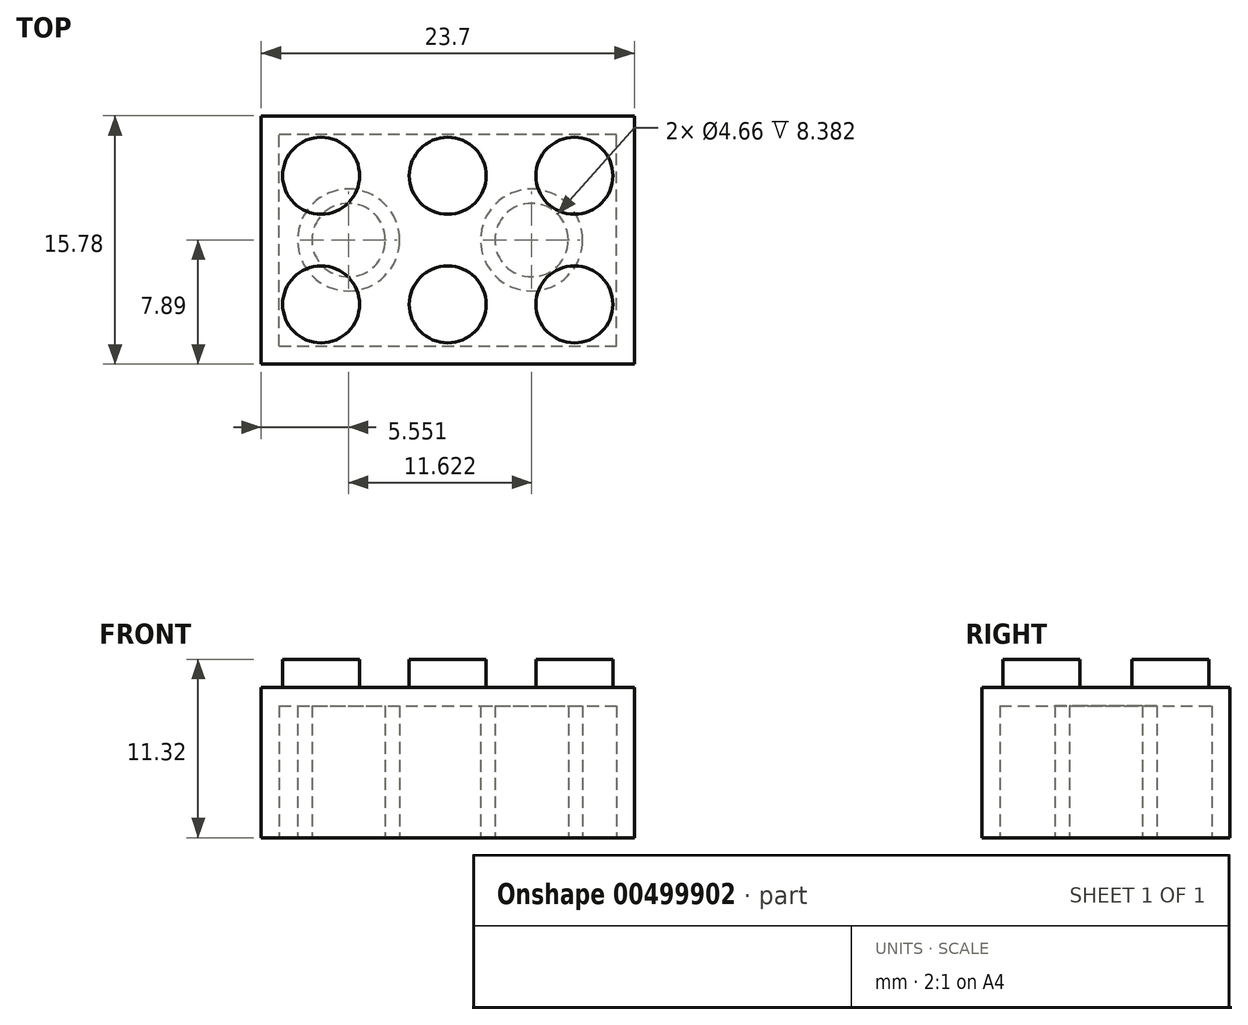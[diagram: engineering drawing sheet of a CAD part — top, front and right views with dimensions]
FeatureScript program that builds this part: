
annotation { "Feature Type Name" : "Feature", "Feature Type Description" : "" }
export const myFeature = defineFeature(function(context is Context, id is Id, definition is map)
    precondition{}
    {
        {
            var Q0;
            Q0=qCreatedBy(makeId("Top.planeOp"),FACE);
            var sketch = newSketch(context, id + "F0", { "sketchPlane" : qUnion([Q0])});
            skLineSegment(sketch, "E0.bottom", {"start": v(-11.85, 7.89) * mm, "end": v(11.85, 7.89) * mm});
            skLineSegment(sketch, "E0.top", {"start": v(-11.85, -7.89) * mm, "end": v(11.85, -7.89) * mm});
            skLineSegment(sketch, "E0.left", {"start": v(-11.85, 7.89) * mm, "end": v(-11.85, -7.89) * mm});
            skLineSegment(sketch, "E0.right", {"start": v(11.85, 7.89) * mm, "end": v(11.85, -7.89) * mm});
            skPoint(sketch, "E0.middle", {"position": v(0, 0) * mm});
            skSolve(sketch);
        }
        {
            var Q0;
            Q0 = qSketchRegion(id + "F0", true);
            extrude(context, id + "F1", {"entities" : qUnion([Q0]), "depth" : 9.54 * mm});
        }
        {
            var Q0;
            Q0=makeQuery(id+"F1.opExtrude","CAP_FACE",FACE,{"disambiguationData":[OSD([sQuery(id+"F0.wireOp",EDGE,"E0.bottom"),sQuery(id+"F0.wireOp",EDGE,"E0.top"),sQuery(id+"F0.wireOp",EDGE,"E0.left"),sQuery(id+"F0.wireOp",EDGE,"E0.right")])],"isStart":false});
            var sketch = newSketch(context, id + "F2", { "sketchPlane" : qUnion([Q0])});
            skCircle(sketch, "E1", {"center": v(-8.05, 4.08) * mm, "radius": 2.44 * mm});
            skCircle(sketch, "E2", {"center": v(0, 4.08) * mm, "radius": 2.44 * mm});
            skCircle(sketch, "E3", {"center": v(8.05, 4.08) * mm, "radius": 2.44 * mm});
            skCircle(sketch, "E4", {"center": v(8.05, -4.08) * mm, "radius": 2.44 * mm});
            skCircle(sketch, "E5", {"center": v(0, -4.08) * mm, "radius": 2.44 * mm});
            skCircle(sketch, "E6", {"center": v(-8.05, -4.08) * mm, "radius": 2.44 * mm});
            skSolve(sketch);
        }
        {
            var Q0;
            Q0=makeQuery(id+"F2.imprint","IMPRINT",FACE,{"disambiguationData":[TD([[makeQuery(id+"F2.imprint","IMPRINT",EDGE,{"derivedFrom":sQuery(id+"F2.wireOp",EDGE,"E6")}),1.0]])]});
            var Q1;
            Q1=makeQuery(id+"F2.imprint","IMPRINT",FACE,{"disambiguationData":[TD([[makeQuery(id+"F2.imprint","IMPRINT",EDGE,{"derivedFrom":sQuery(id+"F2.wireOp",EDGE,"E5")}),1.0]])]});
            var Q2;
            Q2=makeQuery(id+"F2.imprint","IMPRINT",FACE,{"disambiguationData":[TD([[makeQuery(id+"F2.imprint","IMPRINT",EDGE,{"derivedFrom":sQuery(id+"F2.wireOp",EDGE,"E4")}),1.0]])]});
            var Q3;
            Q3=makeQuery(id+"F2.imprint","IMPRINT",FACE,{"disambiguationData":[TD([[makeQuery(id+"F2.imprint","IMPRINT",EDGE,{"derivedFrom":sQuery(id+"F2.wireOp",EDGE,"E3")}),1.0]])]});
            var Q4;
            Q4=makeQuery(id+"F2.imprint","IMPRINT",FACE,{"disambiguationData":[TD([[makeQuery(id+"F2.imprint","IMPRINT",EDGE,{"derivedFrom":sQuery(id+"F2.wireOp",EDGE,"E2")}),1.0]])]});
            var Q5;
            Q5=makeQuery(id+"F2.imprint","IMPRINT",FACE,{"disambiguationData":[TD([[makeQuery(id+"F2.imprint","IMPRINT",EDGE,{"derivedFrom":sQuery(id+"F2.wireOp",EDGE,"E1")}),1.0]])]});
            extrude(context, id + "F3", {"entities" : qUnion([Q0, Q1, Q2, Q3, Q4, Q5]), "operationType" : NewBodyOperationType.ADD, "depth" : 1.78 * mm});
        }
        {
            var Q0;
            Q0=makeQuery(id+"F1.opExtrude","CAP_FACE",FACE,{"disambiguationData":[OSD([sQuery(id+"F0.wireOp",EDGE,"E0.bottom"),sQuery(id+"F0.wireOp",EDGE,"E0.top"),sQuery(id+"F0.wireOp",EDGE,"E0.left"),sQuery(id+"F0.wireOp",EDGE,"E0.right")])],"isStart":true});
            var sketch = newSketch(context, id + "F4", { "sketchPlane" : qUnion([Q0])});
            skLineSegment(sketch, "E7.bottom", {"start": v(-10.7, 6.74) * mm, "end": v(10.7, 6.74) * mm});
            skLineSegment(sketch, "E7.top", {"start": v(-10.7, -6.74) * mm, "end": v(10.7, -6.74) * mm});
            skLineSegment(sketch, "E7.left", {"start": v(-10.7, 6.74) * mm, "end": v(-10.7, -6.74) * mm});
            skLineSegment(sketch, "E7.right", {"start": v(10.7, 6.74) * mm, "end": v(10.7, -6.74) * mm});
            skPoint(sketch, "E7.middle", {"position": v(0, 0) * mm});
            skCircle(sketch, "E8", {"center": v(-6.3, 0) * mm, "radius": 3.24 * mm});
            skCircle(sketch, "E9", {"center": v(5.32, 0) * mm, "radius": 3.24 * mm});
            skCircle(sketch, "E10", {"center": v(-6.3, 0) * mm, "radius": 2.33 * mm});
            skCircle(sketch, "E11", {"center": v(5.32, 0) * mm, "radius": 2.33 * mm});
            skSolve(sketch);
        }
        {
            var Q0;
            Q0=makeQuery(id+"F4.imprint","IMPRINT",FACE,{"disambiguationData":[TD([[makeQuery(id+"F4.imprint","IMPRINT",EDGE,{"derivedFrom":sQuery(id+"F4.wireOp",EDGE,"E7.bottom")}),-1.0]])]});
            extrude(context, id + "F5", {"entities" : qUnion([Q0]), "operationType" : NewBodyOperationType.REMOVE, "oppositeDirection" : true, "depth" : 8.38 * mm});
        }
        {
            var Q0;
            Q0=makeQuery(id+"F4.imprint","IMPRINT",FACE,{"disambiguationData":[TD([[makeQuery(id+"F4.imprint","IMPRINT",EDGE,{"derivedFrom":sQuery(id+"F4.wireOp",EDGE,"E10")}),1.0]])]});
            var Q1;
            Q1=makeQuery(id+"F4.imprint","IMPRINT",FACE,{"disambiguationData":[TD([[makeQuery(id+"F4.imprint","IMPRINT",EDGE,{"derivedFrom":sQuery(id+"F4.wireOp",EDGE,"E11")}),1.0]])]});
            extrude(context, id + "F6", {"entities" : qUnion([Q0, Q1]), "operationType" : NewBodyOperationType.REMOVE, "oppositeDirection" : true, "depth" : 8.38 * mm});
        }
    });
